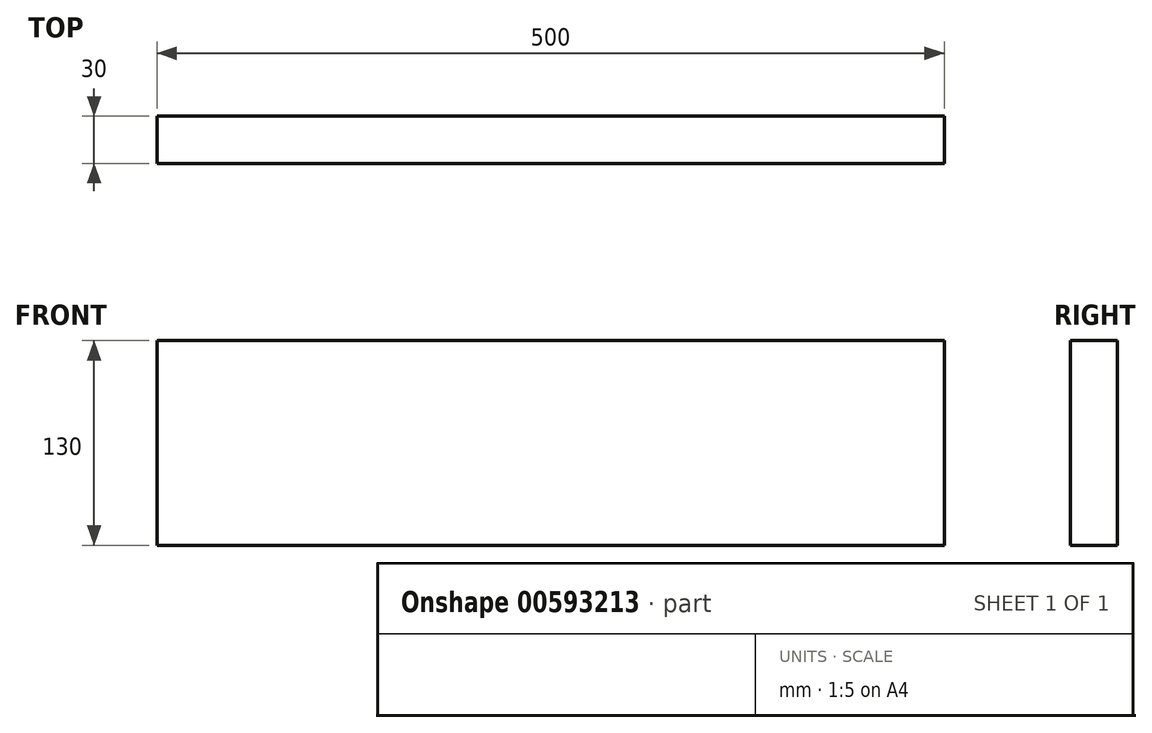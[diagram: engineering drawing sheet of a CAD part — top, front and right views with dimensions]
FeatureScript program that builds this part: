
annotation { "Feature Type Name" : "Feature", "Feature Type Description" : "" }
export const myFeature = defineFeature(function(context is Context, id is Id, definition is map)
    precondition{}
    {
        {
            var Q0;
            Q0=qCreatedBy(makeId("Front.planeOp"),FACE);
            var sketch = newSketch(context, id + "F0", { "sketchPlane" : qUnion([Q0])});
            skLineSegment(sketch, "E0.bottom", {"start": v(-250, 65) * mm, "end": v(250, 65) * mm});
            skLineSegment(sketch, "E0.top", {"start": v(-250, -65) * mm, "end": v(250, -65) * mm});
            skLineSegment(sketch, "E0.left", {"start": v(-250, 65) * mm, "end": v(-250, -65) * mm});
            skLineSegment(sketch, "E0.right", {"start": v(250, 65) * mm, "end": v(250, -65) * mm});
            skPoint(sketch, "E0.middle", {"position": v(0, 0) * mm});
            skSolve(sketch);
        }
        {
            var Q0;
            Q0=makeQuery(id+"F0.imprint","IMPRINT",FACE,{"disambiguationData":[TD([[makeQuery(id+"F0.imprint","IMPRINT",EDGE,{"derivedFrom":sQuery(id+"F0.wireOp",EDGE,"E0.bottom")}),-1.0]])]});
            extrude(context, id + "F1", {"entities" : qUnion([Q0]), "depth" : 30 * mm, "offsetDistance" : 25 * mm});
        }
    });
